# Revit family: bimlib_narujnyeblokisistemakondicionirovaniya_mrv-s-ii_4-5hp_haier
name_source: partatom
category: Оборудование
units: mm (PartAtom-declared; Revit-internal decimal feet)

## family parameters
Всегда вертикально = Да
На основе рабочей плоскости = Нет
Общий = Нет
При загрузке вырезать с полостями = Нет
Размер круглого соединителя = Использовать диаметр
Тип детали = Нормальный
Точка расчета площади = Нет

## types (2) — shared parameters
ADSK_URL документации изделия = https://haierproff.ru
ADSK_URL страницы изделия = https://haierproff.ru
ADSK_Версия Revit = 2017
ADSK_Группирование = VRF-системы MRV-S''
ADSK_Единица измерения = шт.
ADSK_Завод-изготовитель = Haier Group
ADSK_Классификация нагрузок = ОВК
ADSK_Количество = 1
ADSK_Количество фаз = 1
ADSK_Коэффициент мощности = 1
ADSK_Масса = 90
ADSK_Напряжение = 230 В
ADSK_Обозначение = MRV-S'' серия AU
ADSK_Размер_Высота = 965 мм
ADSK_Размер_Глубина = 370 мм
ADSK_Размер_Ширина = 950 мм
ADSK_Расход воздуха = 5400.0 м³/ч
BL_BIM library = https://bimlib.pro
HG_URL поставщика = www.haierproff.ru
URL = www.haier.com
Диаметр_Газ = 15.88 мм
Диаметр_Жидкость = 9.52 мм
Заправка хладагента = 3.30 кг
Изготовитель = Haier Group
Производитель компрессора = MITSUBISHI ELECTRIC
Работа на обогрев = Нет
Рабочий диапазон_Обогрев = -15~ 21
Рабочий диапазон_Охлаждение = -5 ~ 50
Тип компрессора = Роторный
Тип хладагента = R410A
Частота тока = 50 Гц
zero-valued in all types: Отметка по умолчанию

## per-type parameters (varying)
| type | ADSK_Код изделия | ADSK_Наименование | ADSK_Наименование краткое | ADSK_Номинальная мощность | ADSK_Полная мощность | Звуковое давление_Нагрев | Звуковое давление_Охлаждение | Обогрев_Потребляемая мощность | Охлаждение_Потребляемая мощность | Теплопроизводительность | Холодопроизводительность |
| AU042FNERA_4HP_HAIER | AU042FNERA | Наружный блок VRF-системы кондиционирования MRV - S'', 4HP | VRF-системы MRV - S'', 4HP | 4250 Вт | 4250 В·А | 60 | 58 | 4 кВт | 4 кВт | 12 кВт | 12 кВт |
| AU052FNERA_5HP_HAIER | AU052FNERA | Наружный блок VRF-системы кондиционирования MRV - S'', 5HP | VRF-системы MRV - S'', 5HP | 5000 Вт | 5000 В·А | 62 | 60 | 5 кВт | 5 кВт | 14 кВт | 14 кВт |
